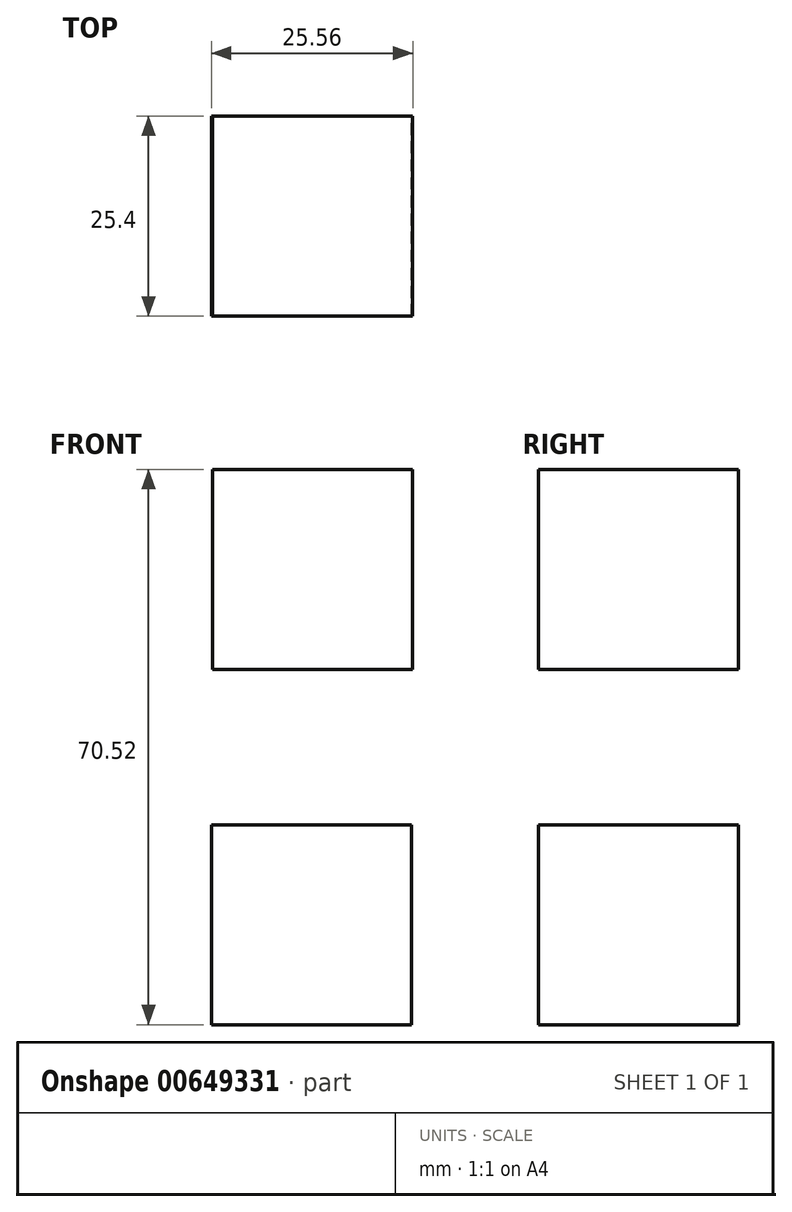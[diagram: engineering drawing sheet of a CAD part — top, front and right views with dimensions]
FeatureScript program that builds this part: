
annotation { "Feature Type Name" : "Feature", "Feature Type Description" : "" }
export const myFeature = defineFeature(function(context is Context, id is Id, definition is map)
    precondition{}
    {
        {
            var Q0;
            Q0=qCreatedBy(makeId("Front.planeOp"),FACE);
            var sketch = newSketch(context, id + "F0", { "sketchPlane" : qUnion([Q0])});
            skLineSegment(sketch, "E0.bottom", {"start": v(12.73, 12.97) * mm, "end": v(-12.67, 12.97) * mm});
            skLineSegment(sketch, "E0.top", {"start": v(12.73, -12.43) * mm, "end": v(-12.67, -12.43) * mm});
            skLineSegment(sketch, "E0.left", {"start": v(12.73, 12.97) * mm, "end": v(12.73, -12.43) * mm});
            skLineSegment(sketch, "E0.right", {"start": v(-12.67, 12.97) * mm, "end": v(-12.67, -12.43) * mm});
            skSolve(sketch);
        }
        {
            var Q0;
            Q0=qCreatedBy(makeId("Front.planeOp"),FACE);
            var sketch = newSketch(context, id + "F1", { "sketchPlane" : qUnion([Q0])});
            skSolve(sketch);
        }
        {
            var Q0;
            Q0 = qSketchRegion(id + "F1", true);
            var Q1;
            Q1=makeQuery(id+"F0.imprint","IMPRINT",FACE,{"disambiguationData":[TD([[makeQuery(id+"F0.imprint","IMPRINT",EDGE,{"derivedFrom":sQuery(id+"F0.wireOp",EDGE,"E0.bottom")}),1.0]])]});
            extrude(context, id + "F2", {"entities" : qUnion([Q0, Q1]), "depth" : 25.4 * mm, "offsetDistance" : 25.4 * mm});
        }
        {
            var Q0;
            Q0=qCreatedBy(makeId("Front.planeOp"),FACE);
            var sketch = newSketch(context, id + "F3", { "sketchPlane" : qUnion([Q0])});
            skLineSegment(sketch, "E1.bottom", {"start": v(12.89, 58.1) * mm, "end": v(-12.51, 58.1) * mm});
            skLineSegment(sketch, "E1.top", {"start": v(12.89, 32.7) * mm, "end": v(-12.51, 32.7) * mm});
            skLineSegment(sketch, "E1.left", {"start": v(12.89, 58.1) * mm, "end": v(12.89, 32.7) * mm});
            skLineSegment(sketch, "E1.right", {"start": v(-12.51, 58.1) * mm, "end": v(-12.51, 32.7) * mm});
            skSolve(sketch);
        }
        {
            var Q0;
            Q0 = qSketchRegion(id + "F3", true);
            extrude(context, id + "F4", {"entities" : qUnion([Q0]), "depth" : 25.4 * mm, "offsetDistance" : 25.4 * mm});
        }
    });
